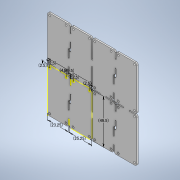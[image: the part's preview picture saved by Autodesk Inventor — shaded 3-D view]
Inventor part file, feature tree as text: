
AUTODESK INVENTOR PART (.ipt)
format: ipt  version: 2021 (Build 250183000, 183)  size: 434,688 bytes
history: native  units: mm
features: sketch x4, extrude x3, fillet x2, other x1, hole x1, pattern_linear x1
ambient origin geometry x8: Origin, YZ Plane, XZ Plane, XY Plane, X Axis, Y Axis, Z Axis, Center Point
bodies: Body1 (feature_tree)
feature tree (12):
  other  "ソリッド1"
  extrude  "押し出し1"  Depth=49.5mm
  extrude  "押し出し2"  Depth=49.5mm
  hole  "穴1"  [1 undecoded]
  pattern_linear  "矩形状パターン1"  Spacing1=1.6mm  [1 undecoded]
  extrude  "押し出し5"  Depth=50.5mm
  fillet  "フィレット3"  Radius=2.5mm
  fillet  "フィレット4"  Radius=2.5mm
  sketch  "スケッチ8"
  sketch  "スケッチ1"
  sketch  "スケッチ3"
  sketch  "スケッチ7"
note: 2 required parameter values undecoded (feature->parameter linkage not recoverable at this tier; creation-order binding heuristic only, values carry confidence <= 0.55)
